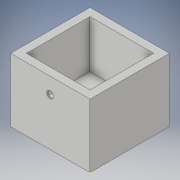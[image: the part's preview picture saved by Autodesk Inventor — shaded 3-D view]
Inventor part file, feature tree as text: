
AUTODESK INVENTOR PART (.ipt)
format: ipt  version: 2019 (Build 230136000, 136)  size: 139,776 bytes
history: native  units: in
note: dims shown in document units (in); Inventor stores cm internally (conversion verified against a paired STEP export)
features: sketch x6, extrude x5, chamfer x1
ambient origin geometry x8: Origin, YZ Plane, XZ Plane, XY Plane, X Axis, Y Axis, Z Axis, Center Point
bodies: Solid1 (feature_tree)
feature tree (12):
  extrude  "Extrusion1"  Depth=5.0in
  extrude  "Extrusion2"  Depth=4.0in
  sketch  "Sketch3"  dims[d5=4.0in d6=0.5in]
  extrude  "Extrusion3"  Depth=0.5in
  extrude  "Extrusion4"  Depth=3.0in
  chamfer  "Chamfer2"  Distance=3.0in
  extrude  "Extrusion5"  Depth=1.0in
  sketch  "Sketch1"  dims[d0=5.0in d1=5.0in]
  sketch  "Sketch2"  dims[d2=4.0in d3=0.0in d4=4.0in]
  sketch  "Sketch4"  dims[d7=0.5in d8=3.0in]
  sketch  "Sketch5"  dims[d9=0.0in]
  sketch  "Sketch6"  dims[d10=0.433in d11=3.0in d12=2.5in d13=3.0in d14=0.0in d15=1.4in d16=2.0in d17=2.0in d18=0.425in d19=0.0in d23=0.425in d24=0.125in d25=30.0deg d26=0.4884in d27=0.4884in d28=2.2558in d29=2.2558in d30=2.2558in d31=2.2558in d32=1.0in d33=0.0in]
